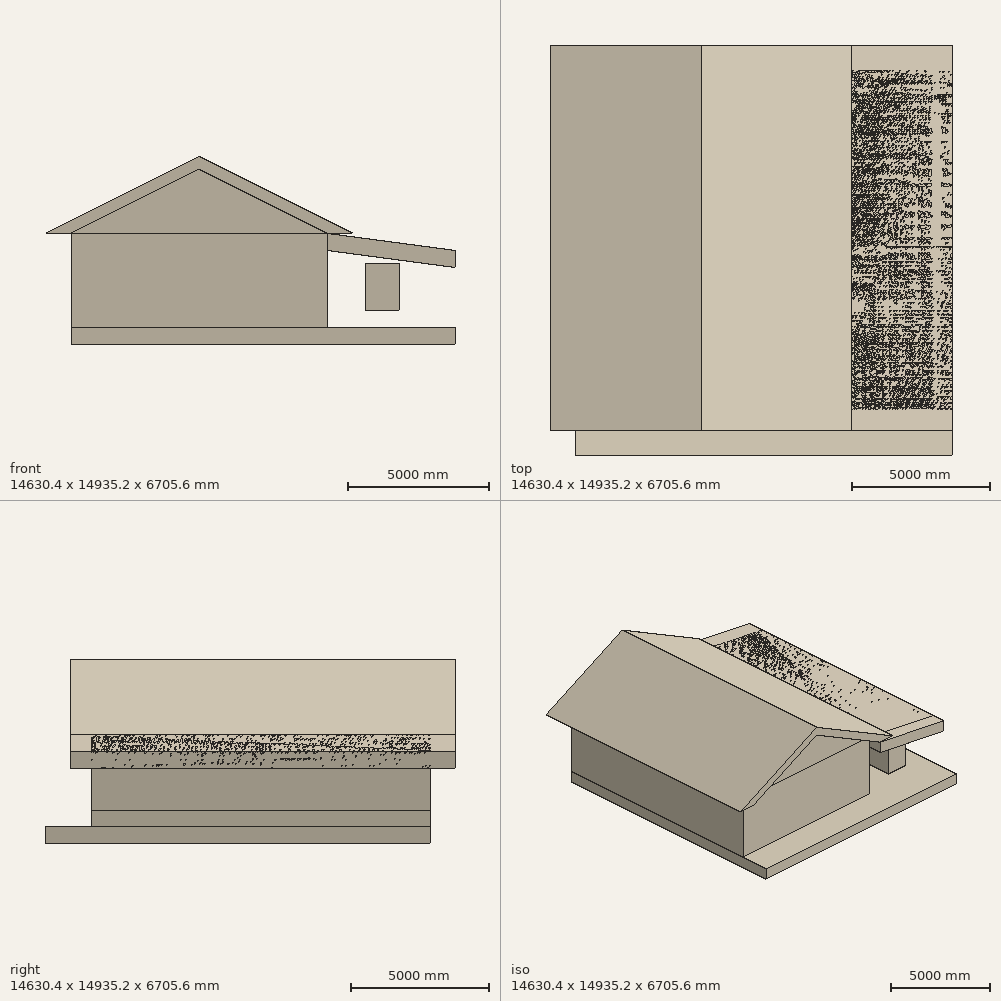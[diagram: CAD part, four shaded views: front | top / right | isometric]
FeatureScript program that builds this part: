
annotation { "Feature Type Name" : "Feature", "Feature Type Description" : "" }
export const myFeature = defineFeature(function(context is Context, id is Id, definition is map)
    precondition{}
    {
        {
            var Q0;
            Q0=qCreatedBy(makeId("Front.planeOp"),FACE);
            var sketch = newSketch(context, id + "F0", { "sketchPlane" : qUnion([Q0])});
            skLineSegment(sketch, "E0", {"start": v(0, 0) * mm, "end": v(-4572, 0) * mm});
            skLineSegment(sketch, "E1", {"start": v(0, 0) * mm, "end": v(4572, 0) * mm});
            skLineSegment(sketch, "E2", {"start": v(4572, 0) * mm, "end": v(5486.4, 0) * mm});
            skLineSegment(sketch, "E3", {"start": v(-4572, 0) * mm, "end": v(-5486.4, 0) * mm});
            skLineSegment(sketch, "E4", {"start": v(0, 0) * mm, "end": v(0, 2286) * mm});
            skLineSegment(sketch, "E5", {"start": v(0, 2286) * mm, "end": v(0, 2743.2) * mm});
            skLineSegment(sketch, "E6", {"start": v(5486.4, 0) * mm, "end": v(0, 2743.2) * mm});
            skLineSegment(sketch, "E7", {"start": v(0, 2286) * mm, "end": v(4572, 0) * mm});
            skLineSegment(sketch, "E8", {"start": v(-4572, 0) * mm, "end": v(0, 2286) * mm});
            skLineSegment(sketch, "E9", {"start": v(-5486.4, 0) * mm, "end": v(0, 2743.2) * mm});
            skLineSegment(sketch, "E10", {"start": v(-4572, 0) * mm, "end": v(-4572, -3352.8) * mm});
            skLineSegment(sketch, "E11", {"start": v(4572, 0) * mm, "end": v(4572, -3352.8) * mm});
            skLineSegment(sketch, "E12", {"start": v(4572, -3352.8) * mm, "end": v(-4572, -3352.8) * mm});
            skLineSegment(sketch, "E13", {"start": v(-4572, -3352.8) * mm, "end": v(-4572, -3962.4) * mm});
            skLineSegment(sketch, "E14", {"start": v(4572, -3352.8) * mm, "end": v(4572, -3962.4) * mm});
            skLineSegment(sketch, "E15", {"start": v(-4572, -3962.4) * mm, "end": v(4572, -3962.4) * mm});
            skLineSegment(sketch, "E16", {"start": v(4572, -3352.8) * mm, "end": v(9144, -3352.8) * mm});
            skLineSegment(sketch, "E17", {"start": v(9144, -3352.8) * mm, "end": v(9144, -3962.4) * mm});
            skLineSegment(sketch, "E18", {"start": v(9144, -3962.4) * mm, "end": v(4572, -3962.4) * mm});
            skLineSegment(sketch, "E19", {"start": v(9144, -3352.8) * mm, "end": v(9144, -609.6) * mm});
            skLineSegment(sketch, "E20", {"start": v(9144, -609.6) * mm, "end": v(4572, 0) * mm});
            skLineSegment(sketch, "E21", {"start": v(4572, 0) * mm, "end": v(4572, -609.6) * mm});
            skLineSegment(sketch, "E22", {"start": v(9144, -609.6) * mm, "end": v(9144, -1219.2) * mm});
            skLineSegment(sketch, "E23", {"start": v(9144, -1219.2) * mm, "end": v(4572, -609.6) * mm});
            skLineSegment(sketch, "E24", {"start": v(-4572, -3352.8) * mm, "end": v(-3352.8, -3352.8) * mm});
            skLineSegment(sketch, "E25", {"start": v(-3352.8, -3352.8) * mm, "end": v(-3352.8, -1219.2) * mm});
            skLineSegment(sketch, "E26", {"start": v(-3352.8, -1219.2) * mm, "end": v(-2438.4, -1219.2) * mm});
            skLineSegment(sketch, "E27", {"start": v(-2438.4, -1219.2) * mm, "end": v(-2438.4, -3352.8) * mm});
            skLineSegment(sketch, "E28.0", {"start": v(-2133.6, -914.4) * mm, "end": v(-2133.6, -3352.8) * mm});
            skLineSegment(sketch, "E28.1", {"start": v(-3657.6, -914.4) * mm, "end": v(-2133.6, -914.4) * mm});
            skLineSegment(sketch, "E28.2", {"start": v(-3657.6, -3352.8) * mm, "end": v(-3657.6, -914.4) * mm});
            skLineSegment(sketch, "E29.bottom", {"start": v(609.6, -1219.2) * mm, "end": v(3352.8, -1219.2) * mm});
            skLineSegment(sketch, "E29.top", {"start": v(609.6, -2590.8) * mm, "end": v(3352.8, -2590.8) * mm});
            skLineSegment(sketch, "E29.left", {"start": v(609.6, -1219.2) * mm, "end": v(609.6, -2590.8) * mm});
            skLineSegment(sketch, "E29.right", {"start": v(3352.8, -1219.2) * mm, "end": v(3352.8, -2590.8) * mm});
            skLineSegment(sketch, "E30.0", {"start": v(457.2, -2743.2) * mm, "end": v(3505.2, -2743.2) * mm});
            skLineSegment(sketch, "E30.1", {"start": v(457.2, -1066.8) * mm, "end": v(457.2, -2743.2) * mm});
            skLineSegment(sketch, "E30.2", {"start": v(457.2, -1066.8) * mm, "end": v(3505.2, -1066.8) * mm});
            skLineSegment(sketch, "E30.3", {"start": v(3505.2, -1066.8) * mm, "end": v(3505.2, -2743.2) * mm});
            skLineSegment(sketch, "E31.bottom", {"start": v(6096, -2590.8) * mm, "end": v(7010.4, -2590.8) * mm});
            skLineSegment(sketch, "E31.top", {"start": v(6096, -1219.2) * mm, "end": v(7010.4, -1219.2) * mm});
            skLineSegment(sketch, "E31.left", {"start": v(6096, -2590.8) * mm, "end": v(6096, -1219.2) * mm});
            skLineSegment(sketch, "E31.right", {"start": v(7010.4, -2590.8) * mm, "end": v(7010.4, -1219.2) * mm});
            skLineSegment(sketch, "E32.0", {"start": v(5943.6, -2743.2) * mm, "end": v(5943.6, -1066.8) * mm});
            skLineSegment(sketch, "E32.1", {"start": v(5943.6, -2743.2) * mm, "end": v(7162.8, -2743.2) * mm});
            skLineSegment(sketch, "E32.2", {"start": v(7162.8, -2743.2) * mm, "end": v(7162.8, -1066.8) * mm});
            skLineSegment(sketch, "E32.3", {"start": v(5943.6, -1066.8) * mm, "end": v(7162.8, -1066.8) * mm});
            skSolve(sketch);
        }
        {
            var Q0;
            Q0=makeQuery(id+"F0.imprint","IMPRINT",FACE,{"disambiguationData":[TD([[makeQuery(id+"F0.imprint","IMPRINT",EDGE,{"derivedFrom":sQuery(id+"F0.wireOp",EDGE,"E3")}),-1.0]])]});
            var Q1;
            Q1=makeQuery(id+"F0.imprint","IMPRINT",FACE,{"disambiguationData":[TD([[makeQuery(id+"F0.imprint","IMPRINT",EDGE,{"derivedFrom":sQuery(id+"F0.wireOp",EDGE,"E2")}),1.0]])]});
            var Q2;
            Q2=makeQuery(id+"F0.imprint","IMPRINT",FACE,{"disambiguationData":[TD([[makeQuery(id+"F0.imprint","IMPRINT",EDGE,{"derivedFrom":sQuery(id+"F0.wireOp",EDGE,"E20")}),1.0]])]});
            extrude(context, id + "F1", {"entities" : qUnion([Q0, Q1, Q2]), "depth" : 914.4 * mm, "offsetDistance" : 30.48 * mm, "hasSecondDirection" : true, "secondDirectionOppositeDirection" : true, "secondDirectionDepth" : 13106.4 * mm});
        }
        {
            var Q0;
            {var subQ0=sQuery(id+"F0.wireOp",EDGE,"E13");Q0=makeQuery(id+"F0.imprint","IMPRINT",FACE,{"disambiguationData":[TD([[makeQuery(id+"F0.imprint","IMPRINT",EDGE,{"derivedFrom":subQ0}),1.0]])]});}
            var Q1;
            Q1=makeQuery(id+"F0.imprint","IMPRINT",FACE,{"disambiguationData":[TD([[makeQuery(id+"F0.imprint","IMPRINT",EDGE,{"derivedFrom":sQuery(id+"F0.wireOp",EDGE,"E14")}),1.0]])]});
            extrude(context, id + "F2", {"entities" : qUnion([Q0, Q1]), "depth" : 1828.8 * mm, "offsetDistance" : 30.48 * mm, "hasSecondDirection" : true, "secondDirectionOppositeDirection" : true, "secondDirectionDepth" : 12192 * mm});
        }
        {
            var Q0;
            Q0=makeQuery(id+"F0.imprint","IMPRINT",FACE,{"disambiguationData":[TD([[makeQuery(id+"F0.imprint","IMPRINT",EDGE,{"derivedFrom":sQuery(id+"F0.wireOp",EDGE,"E0")}),-1.0]])]});
            var Q1;
            Q1=makeQuery(id+"F0.imprint","IMPRINT",FACE,{"disambiguationData":[TD([[makeQuery(id+"F0.imprint","IMPRINT",EDGE,{"derivedFrom":sQuery(id+"F0.wireOp",EDGE,"E1")}),1.0]])]});
            extrude(context, id + "F3", {"entities" : qUnion([Q0, Q1]), "operationType" : NewBodyOperationType.ADD, "depth" : 152.4 * mm, "offsetDistance" : 30.48 * mm, "hasSecondDirection" : true, "secondDirectionOppositeDirection" : true, "secondDirectionDepth" : 12192 * mm});
        }
        {
            var Q0;
            Q0=makeQuery(id+"F0.imprint","IMPRINT",FACE,{"disambiguationData":[TD([[makeQuery(id+"F0.imprint","IMPRINT",EDGE,{"derivedFrom":sQuery(id+"F0.wireOp",EDGE,"E0")}),1.0]])]});
            var Q1;
            {var subQ0=sQuery(id+"F0.wireOp",EDGE,"E25");Q1=makeQuery(id+"F0.imprint","IMPRINT",FACE,{"disambiguationData":[TD([[makeQuery(id+"F0.imprint","IMPRINT",EDGE,{"derivedFrom":subQ0}),1.0]])]});}
            var Q2;
            {var subQ0=sQuery(id+"F0.wireOp",EDGE,"E25");Q2=makeQuery(id+"F0.imprint","IMPRINT",FACE,{"disambiguationData":[TD([[makeQuery(id+"F0.imprint","IMPRINT",EDGE,{"derivedFrom":subQ0}),-1.0]])]});}
            var Q3;
            Q3=makeQuery(id+"F0.imprint","IMPRINT",FACE,{"disambiguationData":[TD([[makeQuery(id+"F0.imprint","IMPRINT",EDGE,{"derivedFrom":sQuery(id+"F0.wireOp",EDGE,"E29.bottom")}),-1.0]])]});
            var Q4;
            Q4=makeQuery(id+"F0.imprint","IMPRINT",FACE,{"disambiguationData":[TD([[makeQuery(id+"F0.imprint","IMPRINT",EDGE,{"derivedFrom":sQuery(id+"F0.wireOp",EDGE,"E29.bottom")}),1.0]])]});
            var Q5;
            Q5=makeQuery(id+"F0.imprint","IMPRINT",FACE,{"disambiguationData":[TD([[makeQuery(id+"F0.imprint","IMPRINT",EDGE,{"derivedFrom":sQuery(id+"F0.wireOp",EDGE,"E11")}),1.0]])]});
            var Q6;
            Q6=makeQuery(id+"F0.imprint","IMPRINT",FACE,{"disambiguationData":[TD([[makeQuery(id+"F0.imprint","IMPRINT",EDGE,{"derivedFrom":sQuery(id+"F0.wireOp",EDGE,"E31.bottom")}),1.0]])]});
            var Q7;
            Q7=makeQuery(id+"F0.imprint","IMPRINT",FACE,{"disambiguationData":[TD([[makeQuery(id+"F0.imprint","IMPRINT",EDGE,{"derivedFrom":sQuery(id+"F0.wireOp",EDGE,"E31.bottom")}),-1.0]])]});
            extrude(context, id + "F4", {"entities" : qUnion([Q0, Q1, Q2, Q3, Q4, Q5, Q6, Q7]), "depth" : 152.4 * mm, "offsetDistance" : 30.48 * mm, "hasSecondDirection" : true, "secondDirectionOppositeDirection" : true, "secondDirectionDepth" : 12192 * mm});
        }
    });
